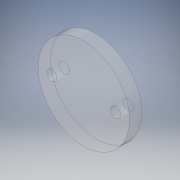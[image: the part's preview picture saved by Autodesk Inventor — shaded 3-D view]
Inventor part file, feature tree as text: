
AUTODESK INVENTOR PART (.ipt)
format: ipt  version: 2019.4 (Build 234330000, 330)  size: 111,104 bytes
history: native  units: mm
features: extrude x1, sketch x1
ambient origin geometry x8: Origin, YZ Plane, XZ Plane, XY Plane, X Axis, Y Axis, Z Axis, Center Point
bodies: Solid1 (feature_tree)
feature tree (2):
  extrude  "Extrusion1"  Depth=3.0mm
  sketch  "Sketch1"  dims[d0=22.0mm d1=15.4mm d2=2.5mm d3=2.5mm d4=3.0mm d5=0.0mm]
